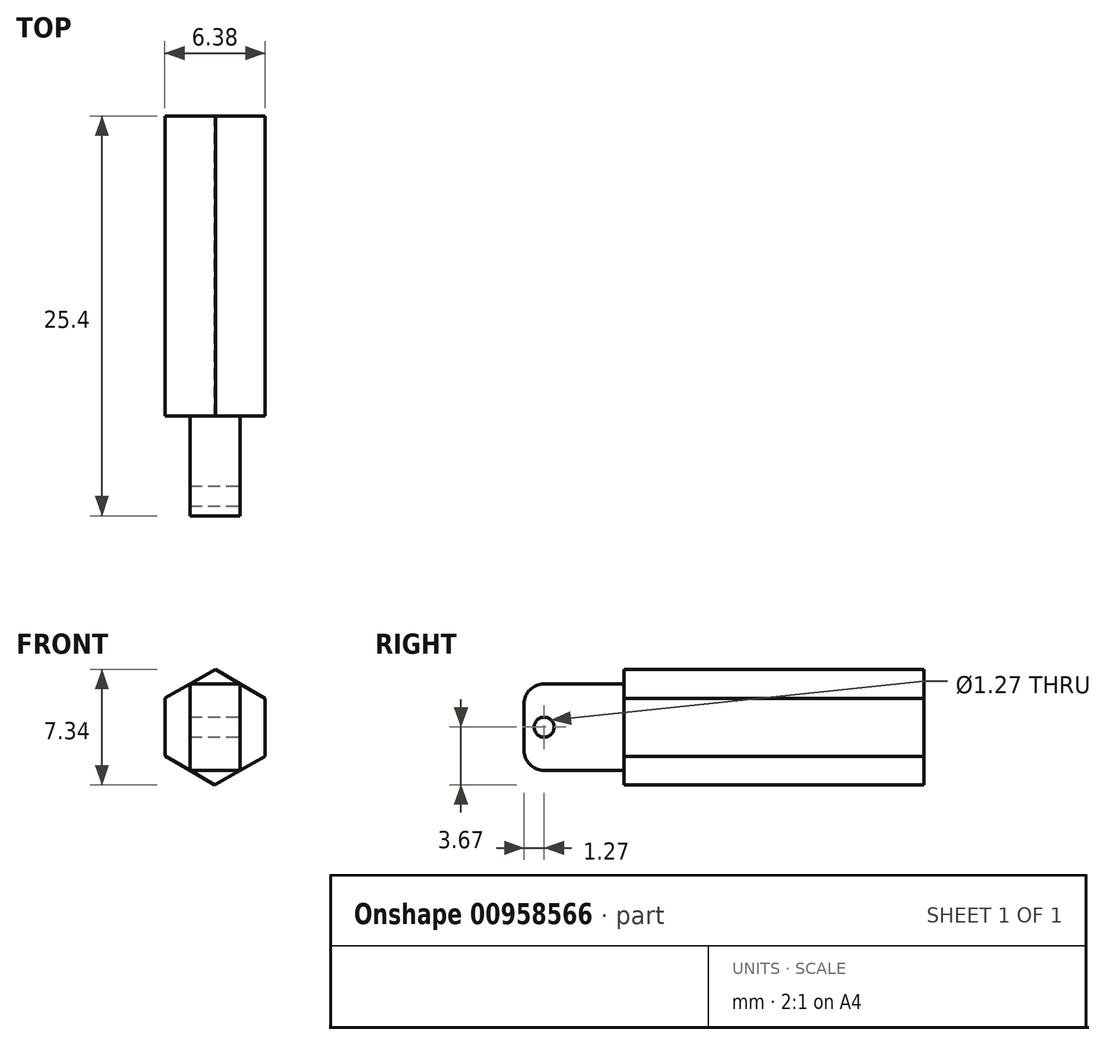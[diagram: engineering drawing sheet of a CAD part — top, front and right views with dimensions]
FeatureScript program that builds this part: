
annotation { "Feature Type Name" : "Feature", "Feature Type Description" : "" }
export const myFeature = defineFeature(function(context is Context, id is Id, definition is map)
    precondition{}
    {
        {
            var Q0;
            Q0=qCreatedBy(makeId("Front.planeOp"),FACE);
            var sketch = newSketch(context, id + "F0", { "sketchPlane" : qUnion([Q0])});
            skCircle(sketch, "E0.cCircle", {"center": v(0, 0) * mm, "radius": 3.18 * mm, "construction": true});
            skLineSegment(sketch, "E0.0", {"start": v(0.02, 3.67) * mm, "end": v(3.19, 1.81) * mm});
            skLineSegment(sketch, "E0.1", {"start": v(3.19, 1.81) * mm, "end": v(3.16, -1.85) * mm});
            skLineSegment(sketch, "E0.2", {"start": v(3.16, -1.85) * mm, "end": v(-0.02, -3.67) * mm});
            skLineSegment(sketch, "E0.3", {"start": v(-0.02, -3.67) * mm, "end": v(-3.19, -1.81) * mm});
            skLineSegment(sketch, "E0.4", {"start": v(-3.19, -1.81) * mm, "end": v(-3.16, 1.85) * mm});
            skLineSegment(sketch, "E0.5", {"start": v(-3.16, 1.85) * mm, "end": v(0.02, 3.67) * mm});
            skPoint(sketch, "E0.0.midPoint", {"position": v(1.6, 2.74) * mm});
            skSolve(sketch);
        }
        {
            var Q0;
            Q0=makeQuery(id+"F0.imprint","IMPRINT",FACE,{"disambiguationData":[TD([[makeQuery(id+"F0.imprint","IMPRINT",EDGE,{"derivedFrom":sQuery(id+"F0.wireOp",EDGE,"E0.0")}),-1.0]])]});
            extrude(context, id + "F1", {"entities" : qUnion([Q0]), "depth" : 19.05 * mm, "offsetDistance" : 25.4 * mm});
        }
        {
            var Q0;
            Q0=makeQuery(id+"F1.opExtrude","CAP_FACE",FACE,{"disambiguationData":[OSD([sQuery(id+"F0.wireOp",EDGE,"E0.0"),sQuery(id+"F0.wireOp",EDGE,"E0.1"),sQuery(id+"F0.wireOp",EDGE,"E0.2"),sQuery(id+"F0.wireOp",EDGE,"E0.3"),sQuery(id+"F0.wireOp",EDGE,"E0.4"),sQuery(id+"F0.wireOp",EDGE,"E0.5")])],"isStart":false});
            var sketch = newSketch(context, id + "F2", { "sketchPlane" : qUnion([Q0])});
            skLineSegment(sketch, "E1.bottom", {"start": v(1.59, 2.75) * mm, "end": v(-1.59, 2.75) * mm});
            skLineSegment(sketch, "E1.top", {"start": v(1.59, -2.75) * mm, "end": v(-1.59, -2.75) * mm});
            skLineSegment(sketch, "E1.left", {"start": v(1.59, 2.75) * mm, "end": v(1.59, -2.75) * mm});
            skLineSegment(sketch, "E1.right", {"start": v(-1.59, 2.75) * mm, "end": v(-1.59, -2.75) * mm});
            skPoint(sketch, "E1.middle", {"position": v(0, 0) * mm});
            skSolve(sketch);
        }
        {
            var Q0;
            Q0=makeQuery(id+"F2.imprint","IMPRINT",FACE,{"disambiguationData":[TD([[makeQuery(id+"F2.imprint","IMPRINT",EDGE,{"derivedFrom":sQuery(id+"F2.wireOp",EDGE,"E1.bottom")}),1.0]])]});
            extrude(context, id + "F3", {"entities" : qUnion([Q0]), "operationType" : NewBodyOperationType.ADD, "depth" : 6.35 * mm, "offsetDistance" : 25.4 * mm});
        }
        {
            var Q0;
            Q0=makeQuery(id+"F3.opExtrude","CAP_EDGE",EDGE,{"disambiguationData":[OSD([sQuery(id+"F2.wireOp",EDGE,"E1.bottom")])],"isStart":false});
            var Q1;
            Q1=makeQuery(id+"F3.opExtrude","CAP_EDGE",EDGE,{"disambiguationData":[OSD([sQuery(id+"F2.wireOp",EDGE,"E1.top")])],"isStart":false});
            fillet(context, id + "F4", {"entities" : qUnion([Q0, Q1]), "radius" : 1.27 * mm, "tangentPropagation" : true, "allowEdgeOverflow" : false});
        }
        {
            var Q0;
            Q0=makeQuery(id+"F3.opExtrude","SWEPT_FACE",FACE,{"disambiguationData":[OSD([sQuery(id+"F2.wireOp",EDGE,"E1.left")])]});
            var sketch = newSketch(context, id + "F5", { "sketchPlane" : qUnion([Q0])});
            skPoint(sketch, "E2", {"position": v(-24.13, 0) * mm});
            skSolve(sketch);
        }
        {
            var Q0;
            Q0=sQuery(id+"F5.wireOp",VERTEX,"E2");
            var Q1;
            Q1=makeQuery(id+"F1.opExtrude","SWEPT_BODY",BODY,{"disambiguationData":[OSD([sQuery(id+"F0.wireOp",EDGE,"E0.0"),sQuery(id+"F0.wireOp",EDGE,"E0.1"),sQuery(id+"F0.wireOp",EDGE,"E0.2"),sQuery(id+"F0.wireOp",EDGE,"E0.3"),sQuery(id+"F0.wireOp",EDGE,"E0.4"),sQuery(id+"F0.wireOp",EDGE,"E0.5")])]});
            hole(context, id + "F6", {"style" : HoleStyle.SIMPLE, "endStyle" : HoleEndStyle.BLIND, "holeDiameter" : 1.27 * mm, "majorDiameter" : 6.35 * mm, "holeDepth" : 25.4 * mm, "isTappedThrough" : true, "tappedDepth" : 12.7 * mm, "tapClearance" : 3, "startFromSketch" : true, "locations" : qUnion([Q0]), "scope" : qUnion([Q1])});
        }
    });
